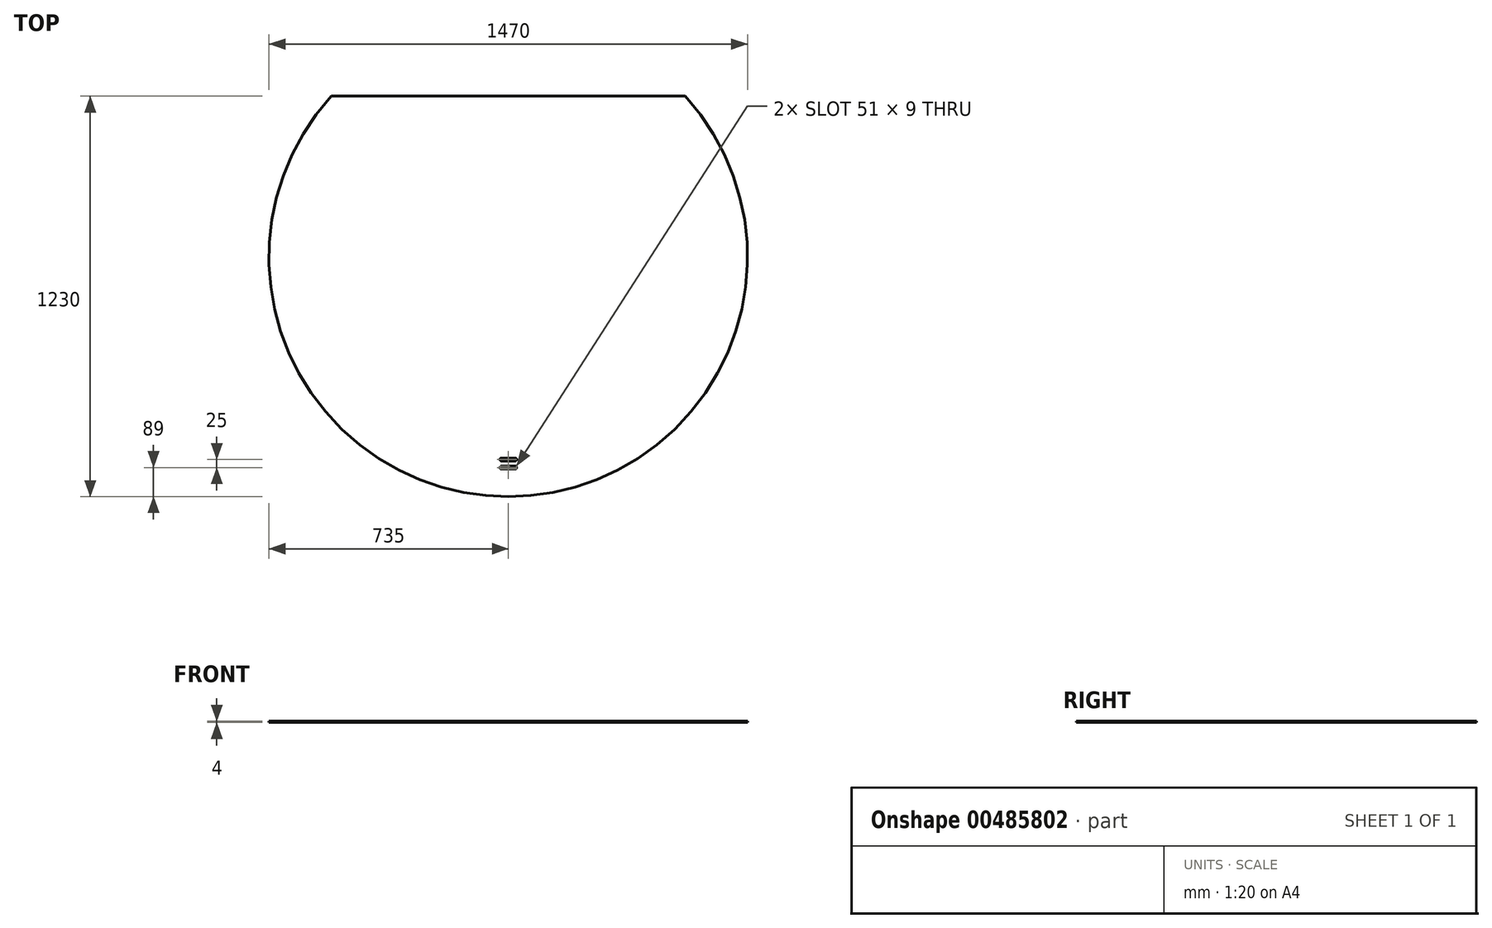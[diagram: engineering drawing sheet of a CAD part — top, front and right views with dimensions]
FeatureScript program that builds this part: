
annotation { "Feature Type Name" : "Feature", "Feature Type Description" : "" }
export const myFeature = defineFeature(function(context is Context, id is Id, definition is map)
    precondition{}
    {
        {
            var Q0;
            Q0=qCreatedBy(makeId("Top.planeOp"),FACE);
            var sketch = newSketch(context, id + "F0", { "sketchPlane" : qUnion([Q0])});
            skArc(sketch, "E0", {"start": v(-543.32, 495) * mm, "mid": v(0, -735) * mm, "end": v(543.32, 495) * mm});
            skLineSegment(sketch, "E1", {"start": v(-543.32, 495) * mm, "end": v(543.32, 495) * mm});
            skSolve(sketch);
        }
        {
            var Q0;
            Q0 = qSketchRegion(id + "F0", true);
            extrude(context, id + "F1", {"entities" : qUnion([Q0]), "depth" : 4 * mm});
        }
        {
            var Q0;
            Q0=makeQuery(id+"F1.opExtrude","CAP_FACE",FACE,{"disambiguationData":[OSD([sQuery(id+"F0.wireOp",EDGE,"E0"),sQuery(id+"F0.wireOp",EDGE,"E1")])],"isStart":false});
            var sketch = newSketch(context, id + "F2", { "sketchPlane" : qUnion([Q0])});
            skLineSegment(sketch, "E2.bottom", {"start": v(-21, -616.5) * mm, "end": v(21, -616.5) * mm});
            skLineSegment(sketch, "E2.top", {"start": v(-21, -625.5) * mm, "end": v(21, -625.5) * mm});
            skArc(sketch, "E3", {"start": v(21, -625.5) * mm, "mid": v(25.5, -621) * mm, "end": v(21, -616.5) * mm});
            skArc(sketch, "E4", {"start": v(-21, -616.5) * mm, "mid": v(-25.5, -621) * mm, "end": v(-21, -625.5) * mm});
            skLineSegment(sketch, "E5.bottom", {"start": v(-21, -641.5) * mm, "end": v(21, -641.5) * mm});
            skLineSegment(sketch, "E5.top", {"start": v(-21, -650.5) * mm, "end": v(21, -650.5) * mm});
            skArc(sketch, "E6", {"start": v(21, -650.5) * mm, "mid": v(25.5, -646) * mm, "end": v(21, -641.5) * mm});
            skArc(sketch, "E7", {"start": v(-21, -641.5) * mm, "mid": v(-25.5, -646) * mm, "end": v(-21, -650.5) * mm});
            skSolve(sketch);
        }
        {
            var Q0;
            Q0 = qSketchRegion(id + "F2", true);
            extrude(context, id + "F3", {"entities" : qUnion([Q0]), "operationType" : NewBodyOperationType.REMOVE, "oppositeDirection" : true, "depth" : 25 * mm});
        }
    });
